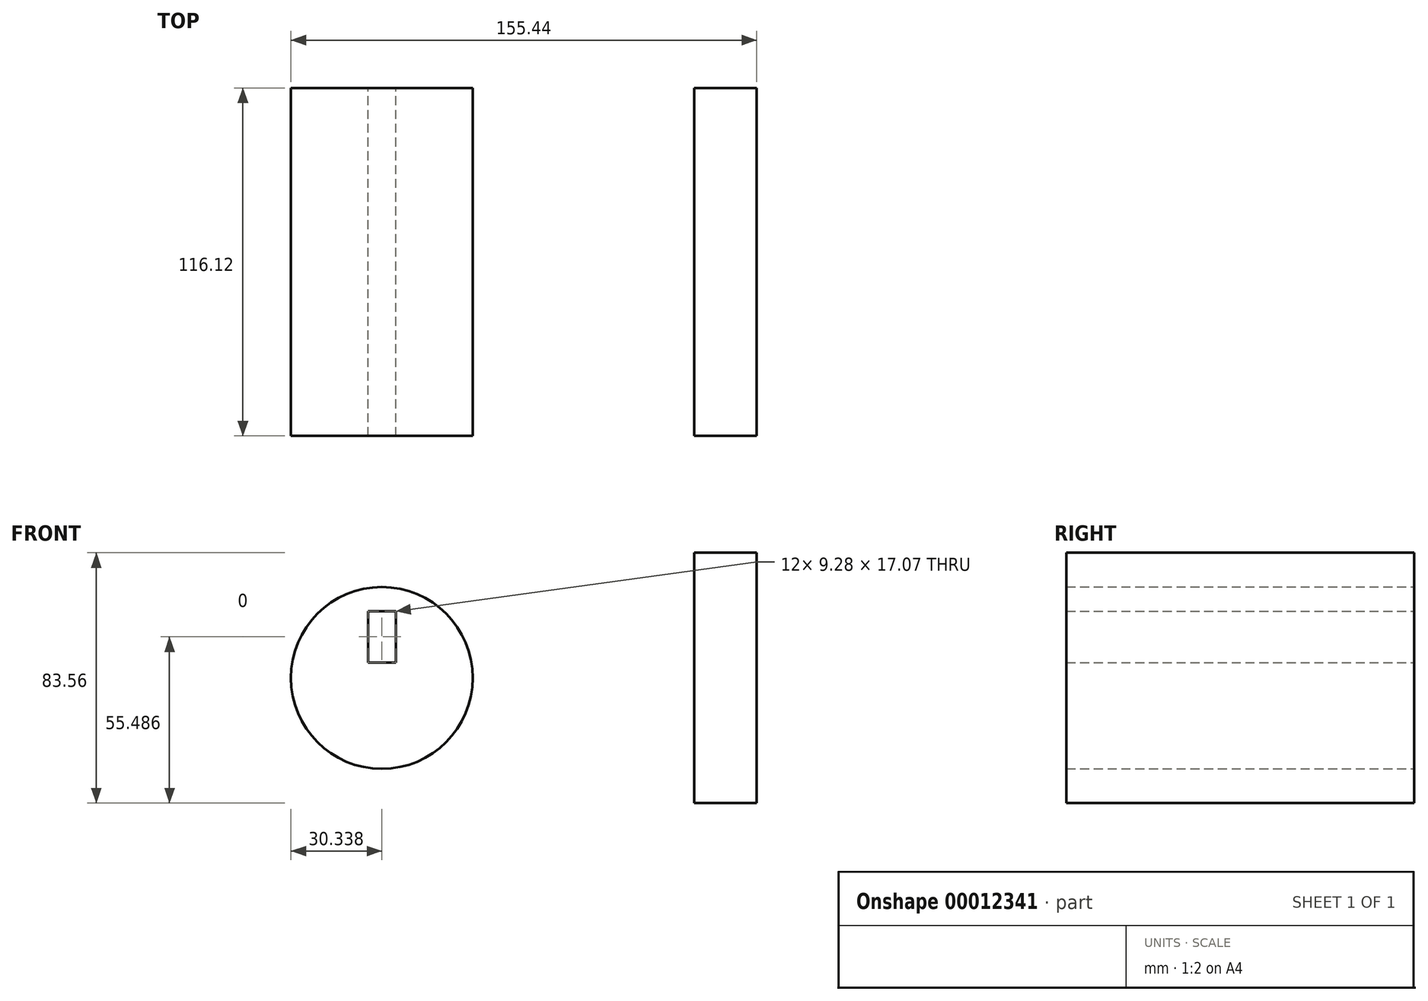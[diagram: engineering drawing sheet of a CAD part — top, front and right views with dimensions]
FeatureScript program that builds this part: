
annotation { "Feature Type Name" : "Feature", "Feature Type Description" : "" }
export const myFeature = defineFeature(function(context is Context, id is Id, definition is map)
    precondition{}
    {
        {
            var Q0;
            Q0=qCreatedBy(makeId("Front.planeOp"),FACE);
            var sketch = newSketch(context, id + "F0", { "sketchPlane" : qUnion([Q0])});
            skCircle(sketch, "E0", {"center": v(-87.23, 0) * mm, "radius": 30.34 * mm});
            skLineSegment(sketch, "E1.rect.bottom", {"start": v(-82.59, 22.24) * mm, "end": v(-91.87, 22.24) * mm});
            skLineSegment(sketch, "E1.rect.top", {"start": v(-82.59, 5.17) * mm, "end": v(-91.87, 5.17) * mm});
            skLineSegment(sketch, "E1.rect.left", {"start": v(-82.59, 22.24) * mm, "end": v(-82.59, 5.17) * mm});
            skLineSegment(sketch, "E1.rect.right", {"start": v(-91.87, 22.24) * mm, "end": v(-91.87, 5.17) * mm});
            skPoint(sketch, "E1.rect.middle", {"position": v(-87.23, 13.7) * mm});
            skLineSegment(sketch, "E2.rect.bottom", {"start": v(37.87, 41.78) * mm, "end": v(16.98, 41.78) * mm});
            skLineSegment(sketch, "E2.rect.top", {"start": v(37.87, -41.78) * mm, "end": v(16.98, -41.78) * mm});
            skLineSegment(sketch, "E2.rect.left", {"start": v(37.87, 41.78) * mm, "end": v(37.87, -41.78) * mm});
            skLineSegment(sketch, "E2.rect.right", {"start": v(16.98, 41.78) * mm, "end": v(16.98, -41.78) * mm});
            skPoint(sketch, "E2.rect.middle", {"position": v(27.43, 0) * mm});
            skLineSegment(sketch, "E3", {"start": v(-87.23, 0) * mm, "end": v(-117.57, 0) * mm, "construction": true});
            skSolve(sketch);
        }
        {
            var Q0;
            Q0=qSketchRegion(id+"F0",true);
            extrude(context, id + "F1", {"entities" : qUnion([Q0]), "endBound" : BoundingType.SYMMETRIC, "depth" : 116.13 * mm});
        }
        {
            var Q0;
            Q0=qCreatedBy(makeId("Front.planeOp"),FACE);
            var sketch = newSketch(context, id + "F2", { "sketchPlane" : qUnion([Q0])});
            skLineSegment(sketch, "E4.0", {"start": v(16.98, 41.78) * mm, "end": v(16.98, -41.78) * mm, "construction": true});
            skLineSegment(sketch, "E5", {"start": v(16.98, 0) * mm, "end": v(-13.36, 0) * mm, "construction": true});
            skSolve(sketch);
        }
    });
